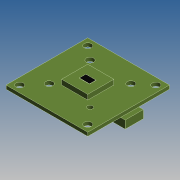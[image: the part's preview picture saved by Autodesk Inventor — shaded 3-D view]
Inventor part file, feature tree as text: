
AUTODESK INVENTOR PART (.ipt)
format: ipt  version: 2019 (Build 230136000, 136)  size: 267,264 bytes
history: native  units: mm
features: sketch x7, extrude x5, hole x1, pattern_circular x1
ambient origin geometry x8: Origin, YZ Plane, XZ Plane, XY Plane, X Axis, Y Axis, Z Axis, Center Point
bodies: Solid1 (feature_tree)
feature tree (14):
  extrude  "Extrusion1"  Depth=36.0mm
  hole  "Hole1"  [1 undecoded]
  pattern_circular  "Circular Pattern1"  Count=4 Angle=360.0deg
  extrude  "Extrusion2"  Depth=2.88mm
  extrude  "Extrusion3"  Depth=11.5mm
  sketch  "Sketch5"  dims[d16=4.512mm d17=2.88mm]
  extrude  "Extrusion4"  Depth=2.2mm TaperAngle=0.0deg
  extrude  "Extrusion5"  Depth=9.0mm
  sketch  "Sketch1"  dims[d0=36.0mm d1=36.0mm]
  sketch  "Sketch2"  dims[d2=1.6mm d3=0.0mm d4=15.0mm]
  sketch  "Sketch3"  dims[d5=15.0mm]
  sketch  "Sketch4"  dims[d6=3.2mm d7=6.0mm d8=4.0mm d9=2.0mm d10=90.0deg d11=8.0mm d12=20.594885mm d13=40.0mm d14=360.0deg]
  sketch  "Sketch6"  dims[d18=2.3mm d19=0.0mm d20=11.5mm]
  sketch  "Sketch7"  dims[d21=11.5mm d22=2.2mm d23=0.0mm d24=9.0mm d25=8.0mm d26=2.0mm d27=3.5mm d28=0.0mm d44=3.2mm d45=3.2mm d46=3.2mm d47=2.3mm d48=10.0mm d49=10.0mm d50=9.0mm d51=9.0mm d52=8.0mm d53=8.0mm d54=18.0mm d55=18.0mm d56=10.0mm d57=0.0mm d58=18.5mm]
note: 1 required parameter value undecoded (feature->parameter linkage not recoverable at this tier; creation-order binding heuristic only, values carry confidence <= 0.55)
